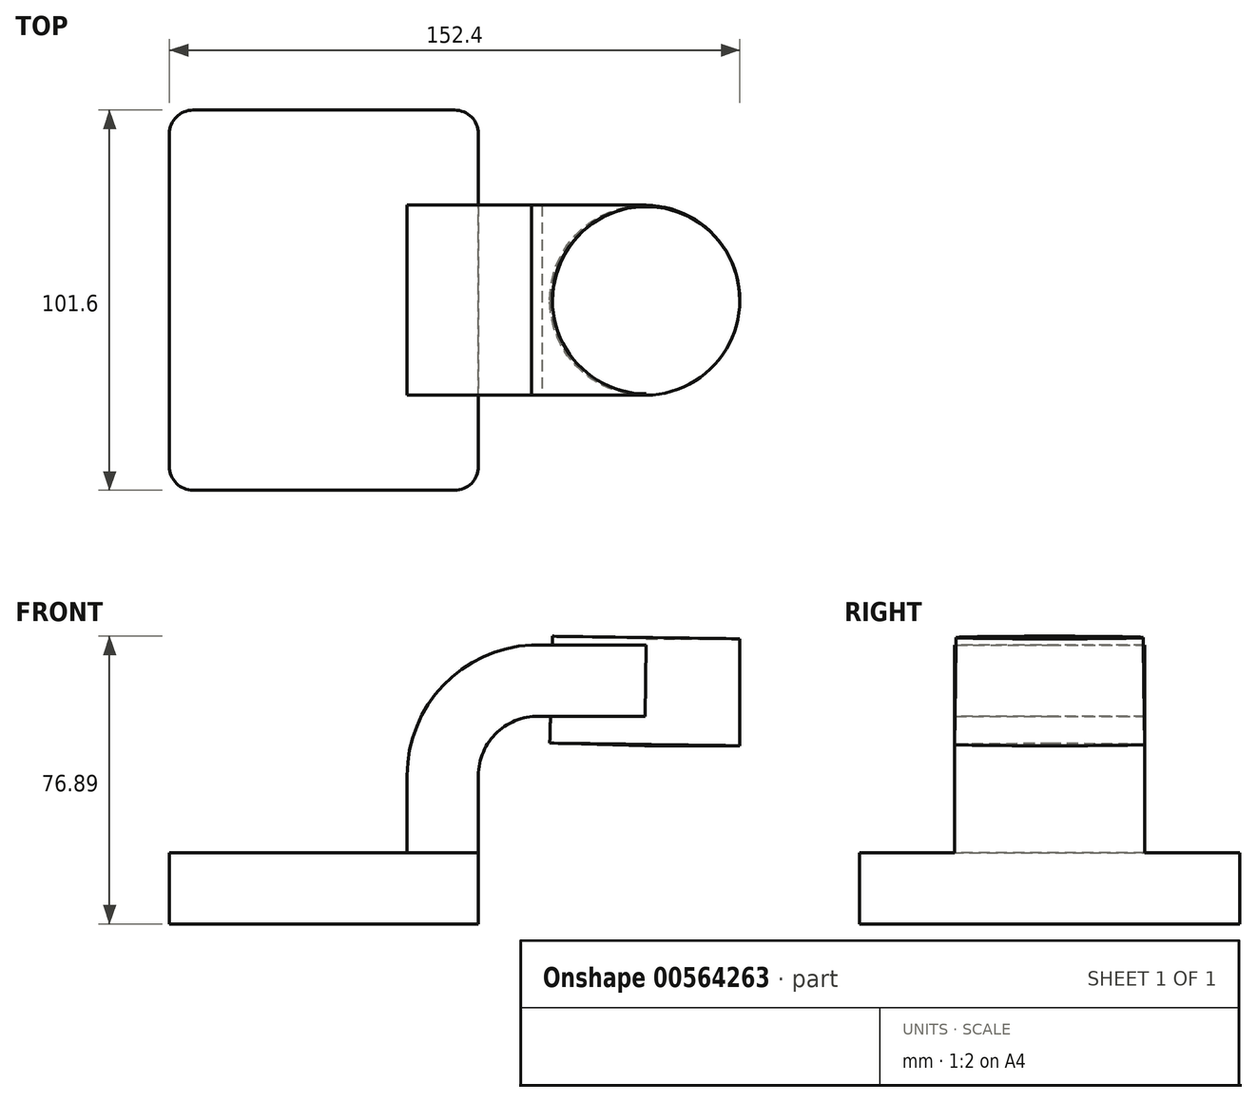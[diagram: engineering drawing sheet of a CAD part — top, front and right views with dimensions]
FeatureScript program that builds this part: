
annotation { "Feature Type Name" : "Feature", "Feature Type Description" : "" }
export const myFeature = defineFeature(function(context is Context, id is Id, definition is map)
    precondition{}
    {
        {
            var Q0;
            Q0=qCreatedBy(makeId("Front.planeOp"),FACE);
            var sketch = newSketch(context, id + "F0", { "sketchPlane" : qUnion([Q0])});
            skLineSegment(sketch, "E0.bottom", {"start": v(-41.28, -9.53) * mm, "end": v(41.28, -9.53) * mm});
            skLineSegment(sketch, "E0.top", {"start": v(-41.28, 9.53) * mm, "end": v(41.28, 9.53) * mm});
            skLineSegment(sketch, "E0.left", {"start": v(-41.28, -9.53) * mm, "end": v(-41.28, 9.52) * mm});
            skLineSegment(sketch, "E0.right", {"start": v(41.28, -9.53) * mm, "end": v(41.28, 9.52) * mm});
            skPoint(sketch, "E0.middle", {"position": v(0, 0) * mm});
            skLineSegment(sketch, "E1.bottom", {"start": v(60.33, 38.1) * mm, "end": v(111.13, 38.1) * mm});
            skLineSegment(sketch, "E1.top", {"start": v(60.33, 66.67) * mm, "end": v(111.13, 66.67) * mm});
            skLineSegment(sketch, "E1.left", {"start": v(60.33, 38.1) * mm, "end": v(60.33, 66.67) * mm});
            skLineSegment(sketch, "E1.right", {"start": v(111.13, 38.1) * mm, "end": v(111.13, 66.67) * mm});
            skPoint(sketch, "E1.middle", {"position": v(85.73, 42.79) * mm});
            skLineSegment(sketch, "E2", {"start": v(41.28, 9.52) * mm, "end": v(41.28, 30.11) * mm});
            skArc(sketch, "E3", {"start": v(41.27, 30.11) * mm, "mid": v(46.32, 41.72) * mm, "end": v(58.24, 45.95) * mm});
            skLineSegment(sketch, "E4", {"start": v(58.24, 45.95) * mm, "end": v(86.11, 45.95) * mm});
            skLineSegment(sketch, "E5.0", {"start": v(55.53, 65) * mm, "end": v(86.11, 65) * mm});
            skArc(sketch, "E5.1", {"start": v(22.23, 30.11) * mm, "mid": v(31.89, 54.23) * mm, "end": v(55.53, 65) * mm});
            skLineSegment(sketch, "E5.2", {"start": v(22.23, 9.52) * mm, "end": v(22.23, 30.11) * mm});
            skLineSegment(sketch, "E6", {"start": v(85.73, 38.1) * mm, "end": v(86.11, 66.67) * mm});
            skFitSpline(sketch, "E7", {"points": [v(55.53, 65) * mm, v(-41.28, 9.53) * mm], "startDerivative": vector(-114.9, -1.12) * mm, "endDerivative": vector(-0.3, -36.16) * mm});
            skSolve(sketch);
        }
        {
            var Q0;
            {var subQ0=sQuery(id+"F0.wireOp",EDGE,"E4");var subQ1=sQuery(id+"F0.wireOp",EDGE,"E1.left");var subQ2=makeQuery(id+"F0.imprint","INTERSECT",VERTEX,{"derivedFrom":[subQ1,subQ0]});Q0=makeQuery(id+"F0.imprint","IMPRINT",FACE,{"disambiguationData":[TD([[makeQuery(id+"F0.imprint","IMPRINT",EDGE,{"disambiguationData":[TD([[subQ2,-1.0]])],"derivedFrom":subQ1}),-1.0]])]});}
            var Q1;
            {var subQ1=sQuery(id+"F0.wireOp",EDGE,"E2");Q1=makeQuery(id+"F0.imprint","IMPRINT",FACE,{"disambiguationData":[TD([[makeQuery(id+"F0.imprint","IMPRINT",EDGE,{"derivedFrom":subQ1}),1.0]])]});}
            extrude(context, id + "F1", {"entities" : qUnion([Q0, Q1]), "endBound" : BoundingType.SYMMETRIC, "oppositeDirection" : true, "depth" : 50.8 * mm, "offsetDistance" : 25.4 * mm});
        }
        {
            var Q0;
            Q0=makeQuery(id+"F0.imprint","IMPRINT",FACE,{"disambiguationData":[TD([[makeQuery(id+"F0.imprint","IMPRINT",EDGE,{"derivedFrom":sQuery(id+"F0.wireOp",EDGE,"E0.bottom")}),1.0]])]});
            extrude(context, id + "F2", {"entities" : qUnion([Q0]), "operationType" : NewBodyOperationType.ADD, "endBound" : BoundingType.SYMMETRIC, "depth" : 101.6 * mm, "offsetDistance" : 25.4 * mm});
        }
        {
            var Q0;
            Q0=makeQuery(id+"F0.imprint","IMPRINT",FACE,{"disambiguationData":[TD([[makeQuery(id+"F0.imprint","IMPRINT",EDGE,{"derivedFrom":sQuery(id+"F0.wireOp",EDGE,"E5.1")}),1.0]])]});
            extrude(context, id + "F3", {"entities" : qUnion([Q0]), "operationType" : NewBodyOperationType.ADD, "endBound" : BoundingType.SYMMETRIC, "depth" : 19.05 * mm, "offsetDistance" : 25.4 * mm});
        }
        {
            var Q0;
            {var subQ0=sQuery(id+"F0.wireOp",EDGE,"E1.right");Q0=makeQuery(id+"F0.imprint","IMPRINT",FACE,{"disambiguationData":[TD([[makeQuery(id+"F0.imprint","IMPRINT",EDGE,{"derivedFrom":subQ0}),1.0]])]});}
            var Q1;
            Q1=sQuery(id+"F0.wireOp",EDGE,"E6");
            revolve(context, id + "F4", {"operationType" : NewBodyOperationType.ADD, "surfaceOperationType" : NewSurfaceOperationType.NEW, "entities" : qUnion([Q0]), "axis" : qUnion([Q1]), "revolveType" : RevolveType.FULL});
        }
        {
            var Q0;
            Q0=makeQuery(id+"F2.opExtrude","CAP_EDGE",EDGE,{"disambiguationData":[OSD([sQuery(id+"F0.wireOp",EDGE,"E0.right")])],"isStart":false});
            var Q1;
            Q1=makeQuery(id+"F2.opExtrude","CAP_EDGE",EDGE,{"disambiguationData":[OSD([sQuery(id+"F0.wireOp",EDGE,"E0.left")])],"isStart":false});
            var Q2;
            Q2=makeQuery(id+"F2.opExtrude","CAP_EDGE",EDGE,{"disambiguationData":[OSD([sQuery(id+"F0.wireOp",EDGE,"E0.right")])],"isStart":true});
            var Q3;
            Q3=makeQuery(id+"F2.opExtrude","CAP_EDGE",EDGE,{"disambiguationData":[OSD([sQuery(id+"F0.wireOp",EDGE,"E0.left")])],"isStart":true});
            fillet(context, id + "F5", {"entities" : qUnion([Q0, Q1, Q2, Q3]), "tangentPropagation" : true, "radius" : 6.35 * mm, "defaultsChanged" : false, "vertexSettings" : [], "allowEdgeOverflow" : false});
        }
    });
